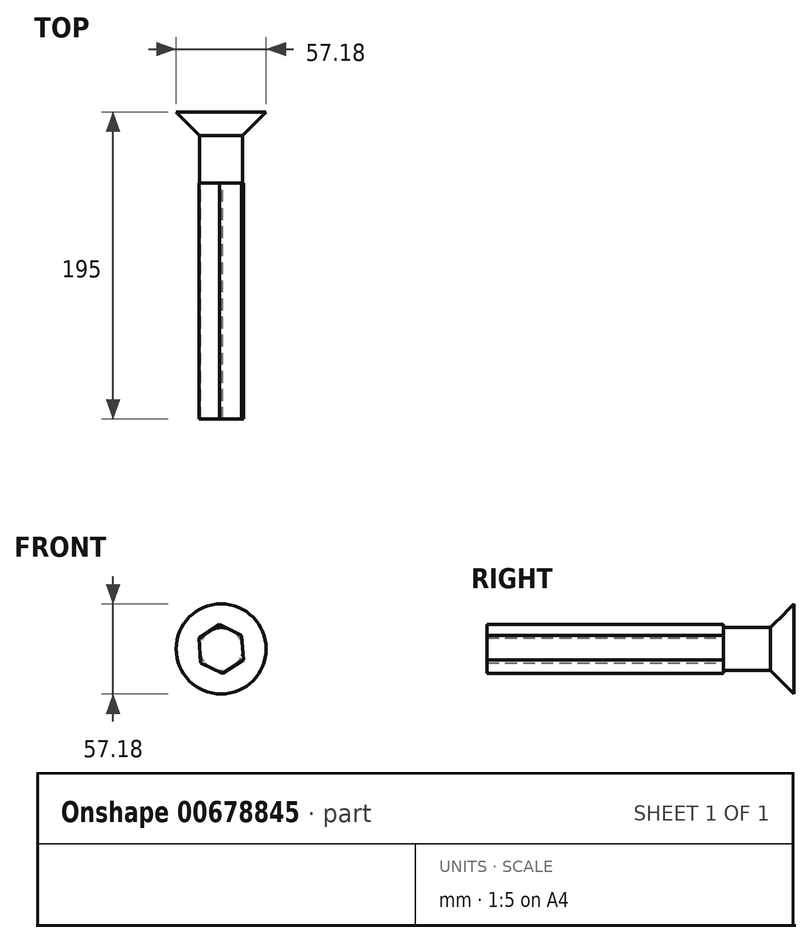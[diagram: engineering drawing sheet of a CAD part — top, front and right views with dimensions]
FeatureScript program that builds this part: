
annotation { "Feature Type Name" : "Feature", "Feature Type Description" : "" }
export const myFeature = defineFeature(function(context is Context, id is Id, definition is map)
    precondition{}
    {
        {
            var Q0;
            Q0=qCreatedBy(makeId("Front.planeOp"),FACE);
            var sketch = newSketch(context, id + "F0", { "sketchPlane" : qUnion([Q0])});
            skLineSegment(sketch, "E0.0", {"start": v(-1.03, 15.66) * mm, "end": v(13.05, 8.72) * mm});
            skLineSegment(sketch, "E0.1", {"start": v(13.05, 8.72) * mm, "end": v(14.08, -6.94) * mm});
            skLineSegment(sketch, "E0.2", {"start": v(14.08, -6.94) * mm, "end": v(1.03, -15.66) * mm});
            skLineSegment(sketch, "E0.3", {"start": v(1.03, -15.66) * mm, "end": v(-13.05, -8.72) * mm});
            skLineSegment(sketch, "E0.4", {"start": v(-13.05, -8.72) * mm, "end": v(-14.08, 6.94) * mm});
            skLineSegment(sketch, "E0.5", {"start": v(-14.08, 6.94) * mm, "end": v(-1.03, 15.66) * mm});
            skSolve(sketch);
        }
        {
            var Q0;
            Q0=makeQuery(id+"F0.imprint","IMPRINT",FACE,{"disambiguationData":[TD([[makeQuery(id+"F0.imprint","IMPRINT",EDGE,{"derivedFrom":sQuery(id+"F0.wireOp",EDGE,"E0.0")}),-1.0]])]});
            extrude(context, id + "F1", {"entities" : qUnion([Q0]), "depth" : 150 * mm, "offsetDistance" : 25 * mm});
        }
        {
            var Q0;
            Q0=makeQuery(id+"F1.opExtrude","CAP_FACE",FACE,{"disambiguationData":[OSD([sQuery(id+"F0.wireOp",EDGE,"E0.0"),sQuery(id+"F0.wireOp",EDGE,"E0.1"),sQuery(id+"F0.wireOp",EDGE,"E0.2"),sQuery(id+"F0.wireOp",EDGE,"E0.3"),sQuery(id+"F0.wireOp",EDGE,"E0.4"),sQuery(id+"F0.wireOp",EDGE,"E0.5")])],"isStart":true});
            var sketch = newSketch(context, id + "F2", { "sketchPlane" : qUnion([Q0])});
            skCircle(sketch, "E1", {"center": v(0, 0) * mm, "radius": 13.6 * mm});
            skSolve(sketch);
        }
        {
            var Q0;
            {var subQ0=sQuery(id+"F2.wireOp",EDGE,"E1");var subQ4=makeQuery(id+"F2.imprint","INTERSECT",VERTEX,{"derivedFrom":[makeQuery(id+"F1.opExtrude","CAP_EDGE",EDGE,{"disambiguationData":[OSD([sQuery(id+"F0.wireOp",EDGE,"E0.0")])],"isStart":true}),subQ0]});Q0=makeQuery(id+"F2.imprint","IMPRINT",FACE,{"disambiguationData":[TD([[makeQuery(id+"F2.imprint","IMPRINT",EDGE,{"disambiguationData":[TD([[subQ4,1.0]])],"derivedFrom":subQ0}),1.0]])]});}
            extrude(context, id + "F3", {"entities" : qUnion([Q0]), "operationType" : NewBodyOperationType.ADD, "depth" : 30 * mm, "offsetDistance" : 25 * mm});
        }
        {
            var Q0;
            Q0=makeQuery(id+"F3.opExtrude","CAP_FACE",FACE,{"disambiguationData":[OSD([sQuery(id+"F2.wireOp",EDGE,"E1")])],"isStart":false});
            extrude(context, id + "F4", {"entities" : qUnion([Q0]), "operationType" : NewBodyOperationType.ADD, "depth" : 15 * mm, "offsetDistance" : 25 * mm, "hasDraft" : true, "draftAngle" : 45 * degree});
        }
    });
